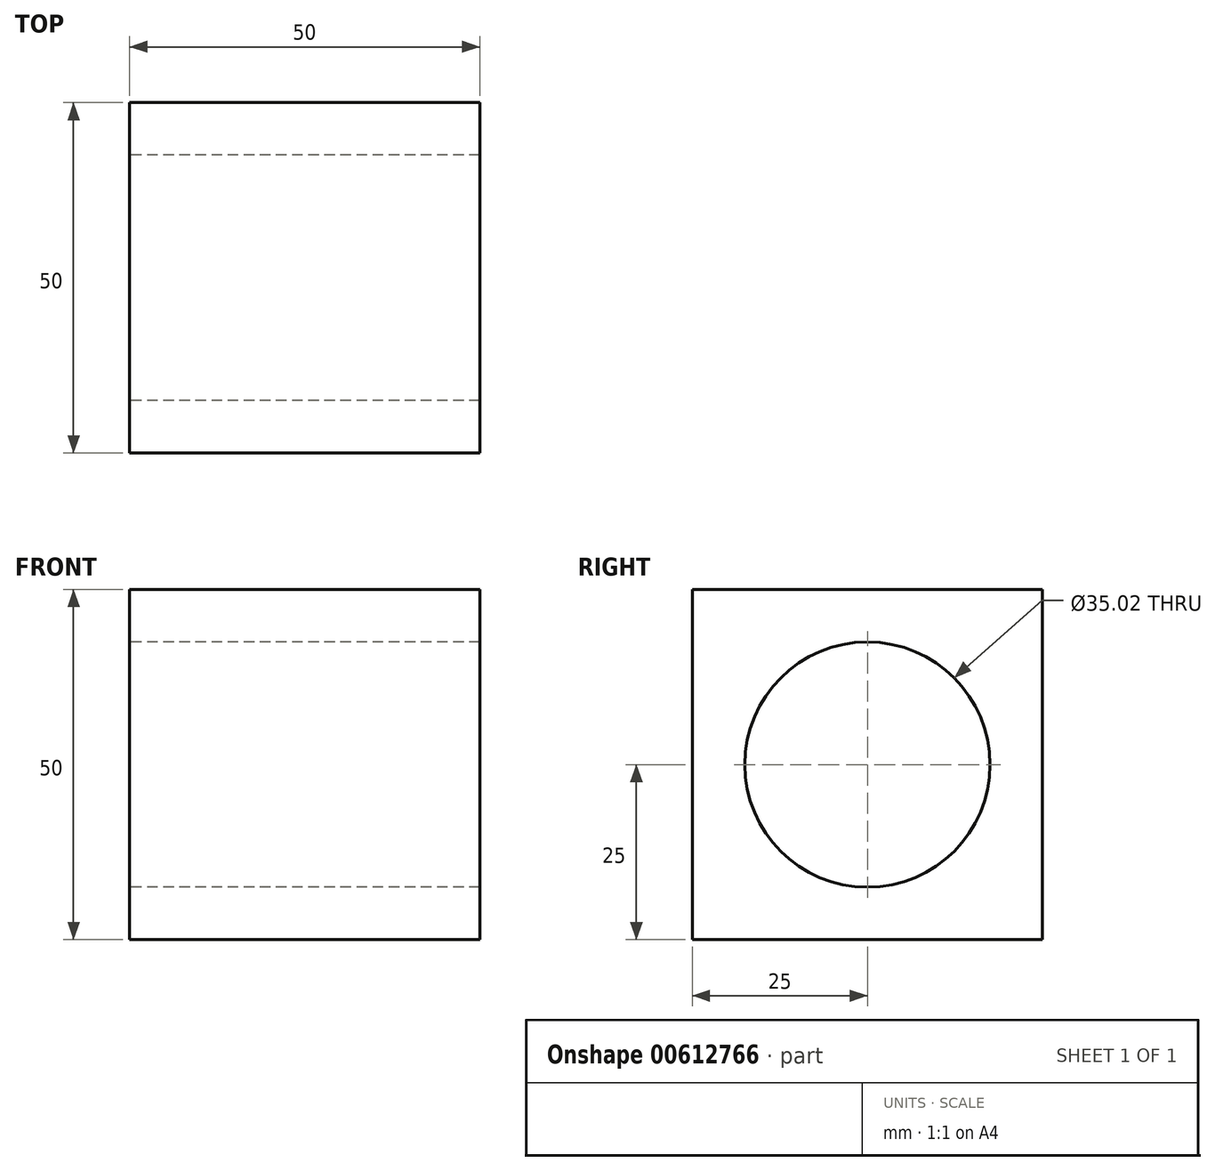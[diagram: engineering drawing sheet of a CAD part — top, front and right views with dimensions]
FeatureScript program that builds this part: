
annotation { "Feature Type Name" : "Feature", "Feature Type Description" : "" }
export const myFeature = defineFeature(function(context is Context, id is Id, definition is map)
    precondition{}
    {
        {
            var Q0;
            Q0=qCreatedBy(makeId("Top.planeOp"),FACE);
            var sketch = newSketch(context, id + "F0", { "sketchPlane" : qUnion([Q0])});
            skLineSegment(sketch, "E0.bottom", {"start": v(0, 0) * mm, "end": v(-50, 0) * mm});
            skLineSegment(sketch, "E0.top", {"start": v(0, 50) * mm, "end": v(-50, 50) * mm});
            skLineSegment(sketch, "E0.left", {"start": v(0, 0) * mm, "end": v(0, 50) * mm});
            skLineSegment(sketch, "E0.right", {"start": v(-50, 0) * mm, "end": v(-50, 50) * mm});
            skSolve(sketch);
        }
        {
            var Q0;
            Q0 = qSketchRegion(id + "F0", true);
            extrude(context, id + "F1", {"entities" : qUnion([Q0]), "depth" : 50 * mm, "offsetDistance" : 25 * mm});
        }
        {
            var Q0;
            Q0=makeQuery(id+"F1.opExtrude","SWEPT_FACE",FACE,{"disambiguationData":[OSD([sQuery(id+"F0.wireOp",EDGE,"E0.right")])]});
            var sketch = newSketch(context, id + "F2", { "sketchPlane" : qUnion([Q0])});
            skCircle(sketch, "E1", {"center": v(-25, 25) * mm, "radius": 17.5 * mm});
            skSolve(sketch);
        }
        {
            var Q0;
            Q0=makeQuery(id+"F2.imprint","IMPRINT",FACE,{"disambiguationData":[TD([[makeQuery(id+"F2.imprint","IMPRINT",EDGE,{"derivedFrom":sQuery(id+"F2.wireOp",EDGE,"E1")}),1.0]])]});
            extrude(context, id + "F3", {"entities" : qUnion([Q0]), "operationType" : NewBodyOperationType.REMOVE, "oppositeDirection" : true, "depth" : 50 * mm, "offsetDistance" : 25 * mm});
        }
    });
